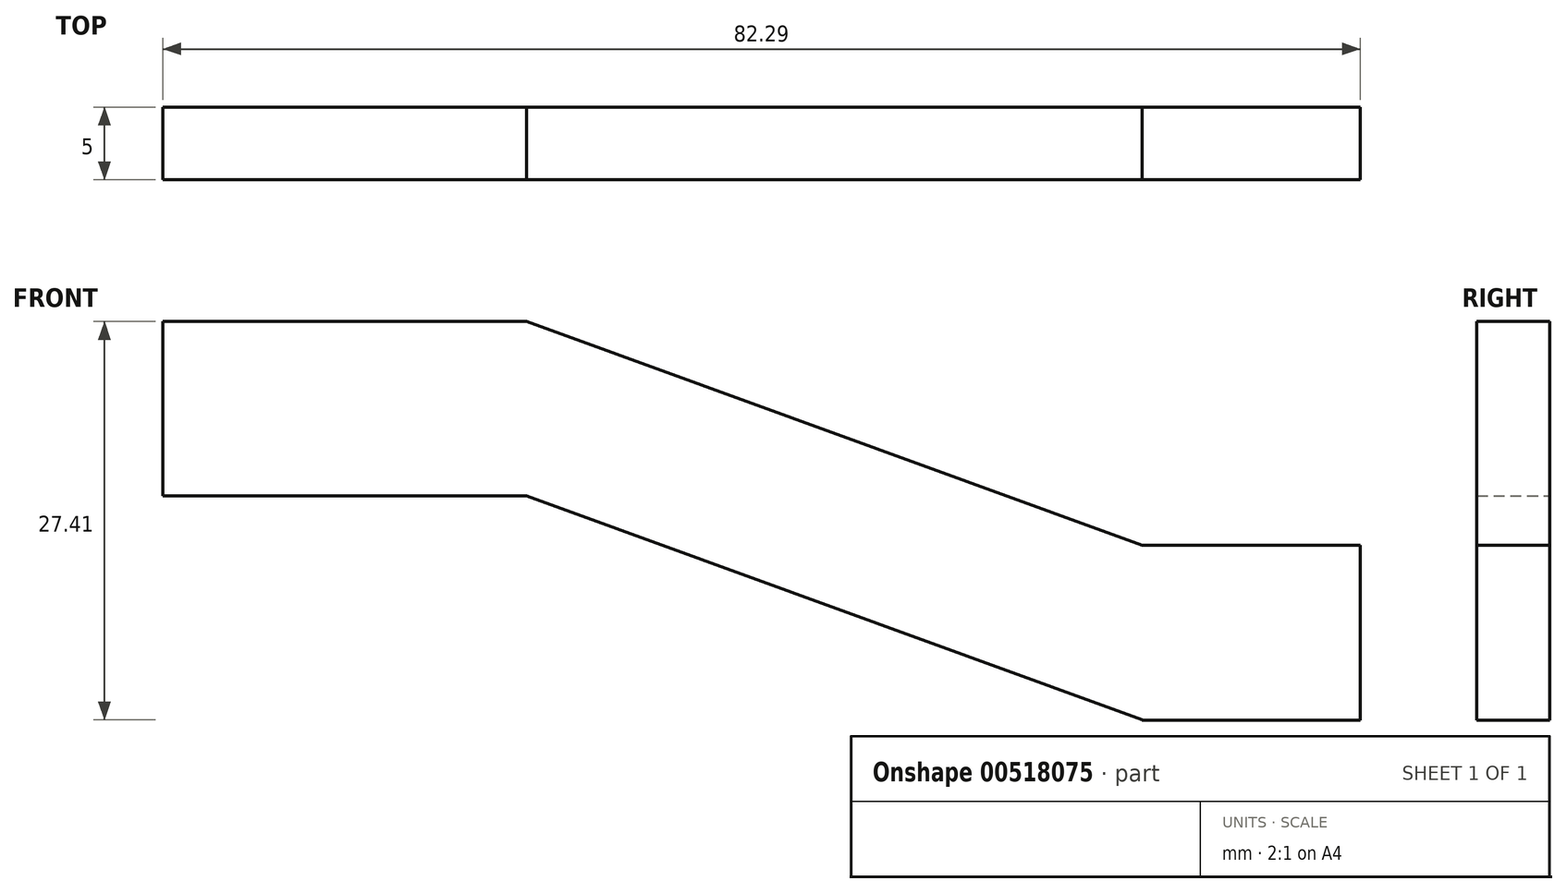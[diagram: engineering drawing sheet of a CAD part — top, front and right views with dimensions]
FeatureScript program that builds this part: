
annotation { "Feature Type Name" : "Feature", "Feature Type Description" : "" }
export const myFeature = defineFeature(function(context is Context, id is Id, definition is map)
    precondition{}
    {
        {
            var Q0;
            Q0=qCreatedBy(makeId("Front.planeOp"),FACE);
            var sketch = newSketch(context, id + "F0", { "sketchPlane" : qUnion([Q0])});
            skLineSegment(sketch, "E0.bottom", {"start": v(0, 0) * mm, "end": v(25, 0) * mm});
            skLineSegment(sketch, "E0.top", {"start": v(0, -12) * mm, "end": v(25, -12) * mm});
            skLineSegment(sketch, "E0.left", {"start": v(0, 0) * mm, "end": v(0, -12) * mm});
            skLineSegment(sketch, "E0.right", {"start": v(25, 0) * mm, "end": v(25, -12) * mm});
            skLineSegment(sketch, "E1", {"start": v(25, -12) * mm, "end": v(67.29, -27.4) * mm});
            skLineSegment(sketch, "E2", {"start": v(25, 0) * mm, "end": v(67.29, -15.4) * mm});
            skLineSegment(sketch, "E3", {"start": v(67.29, -16.7) * mm, "end": v(67.29, -15.4) * mm});
            skLineSegment(sketch, "E4", {"start": v(67.29, -15.4) * mm, "end": v(67.29, -27.4) * mm});
            skLineSegment(sketch, "E5.bottom", {"start": v(67.29, -15.4) * mm, "end": v(82.29, -15.4) * mm});
            skLineSegment(sketch, "E5.top", {"start": v(67.29, -27.41) * mm, "end": v(82.29, -27.41) * mm});
            skLineSegment(sketch, "E5.left", {"start": v(67.29, -15.4) * mm, "end": v(67.29, -27.41) * mm});
            skLineSegment(sketch, "E5.right", {"start": v(82.29, -15.4) * mm, "end": v(82.29, -27.41) * mm});
            skSolve(sketch);
        }
        {
            var Q0;
            Q0 = qSketchRegion(id + "F0", true);
            extrude(context, id + "F1", {"entities" : qUnion([Q0]), "depth" : 5 * mm, "offsetDistance" : 25 * mm});
        }
    });
